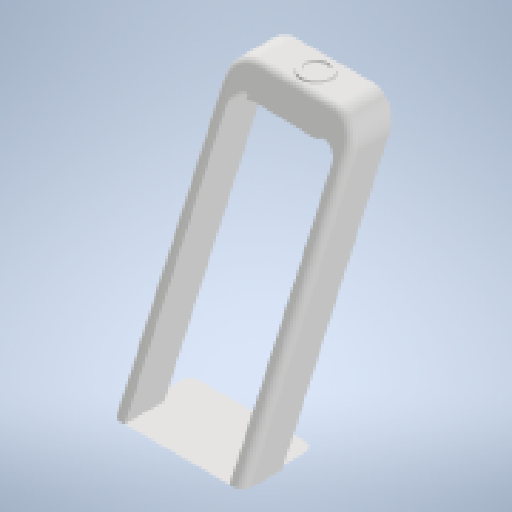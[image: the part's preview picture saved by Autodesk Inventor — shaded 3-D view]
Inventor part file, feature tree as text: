
AUTODESK INVENTOR PART (.ipt)
format: ipt  version: 2024 (Build 280153000, 153)  size: 725,504 bytes
history: native  units: in
note: dims shown in document units (in); Inventor stores cm internally (conversion verified against a paired STEP export)
features: fillet x17, extrude x9, sketch x9
ambient origin geometry x8: Origin, YZ Plane, XZ Plane, XY Plane, X Axis, Y Axis, Z Axis, Center Point
bodies: Solid1 (feature_tree)
feature tree (35):
  extrude  "Extrusion1"  Depth=0.1in
  extrude  "Extrusion2"  Depth=100.0in
  extrude  "Extrusion3"  Depth=50.0in TaperAngle=0.0deg
  fillet  "Fillet1"  Radius=5.0in
  extrude  "Extrusion4"  Depth=15.0in
  extrude  "Extrusion5"  Depth=50.0in TaperAngle=0.0deg
  extrude  "Extrusion6"  Depth=5.0in
  extrude  "Extrusion7"  Depth=90.0in
  fillet  "Fillet6"  Radius=90.0in
  fillet  "Fillet7"  Radius=6.0in
  fillet  "Fillet8"  [1 undecoded]
  extrude  "Extrusion8"  Depth=3.0in TaperAngle=0.0deg
  fillet  "Fillet9"  Radius=6.0in
  fillet  "Fillet10"  Radius=0.7in
  fillet  "Fillet11"  Radius=40.0in
  fillet  "Fillet12"  Radius=40.0in
  fillet  "Fillet13"  Radius=5.0in
  fillet  "Fillet15"  Radius=2.0in
  fillet  "Fillet17"  Radius=3.0in
  fillet  "Fillet18"  Radius=8.0in
  fillet  "Fillet19"  Radius=15.0in
  fillet  "Fillet20"  Radius=12.0in
  extrude  "Extrusion9"  Depth=3.0in TaperAngle=0.0deg
  fillet  "Fillet21"  Radius=1.9375in
  fillet  "Fillet22"  Radius=7.0in
  fillet  "Fillet23"  Radius=5.0in
  sketch  "Sketch2"  dims[d0=50.0in d1=0.1in]
  sketch  "Sketch3"  dims[d2=35.0in d3=0.0in d4=100.0in]
  sketch  "Sketch4"  dims[d5=0.0in d6=50.0in d7=0.0in d8=5.0in]
  sketch  "Sketch5"  dims[d9=50.0in d10=15.0in]
  sketch  "Sketch9"  dims[d11=15.0in d12=50.0in d13=0.0in]
  sketch  "Sketch10"  dims[d14=10.0in d15=5.0in]
  sketch  "Sketch11"  dims[d16=5.0in d18=90.0in d19=90.0in]
  sketch  "Sketch12"  dims[d20=40.0in d21=37.625in d22=0.0in d23=0.0in d34=6.0in d35=0.0in]
  sketch  "Sketch13"  dims[d36=0.5in d37=40.0in d38=0.5in d39=0.0in d40=0.0in d41=6.0in d42=0.7in d43=40.0in d44=0.5in d45=0.0in d46=0.0in d47=40.0in d48=20.0in d49=0.0in d50=0.0in d51=5.0in d52=2.0in d53=3.0in d54=8.0in d55=15.0in d56=12.0in d57=1.0in d58=0.0in d59=1.9375in d60=7.0in d61=5.0in d62=5.0in d63=5.0in d64=5.0in d66=2.0in d68=8.0in d69=5.0in d70=8.0in d71=8.0in d72=40.0in d73=0.3in d74=0.0in d75=10.0in d76=0.05in d77=3.0in d25=0.0in d26=0.0in d27=0.0in d28=0.0in]
note: 1 required parameter value undecoded (feature->parameter linkage not recoverable at this tier; creation-order binding heuristic only, values carry confidence <= 0.55)
